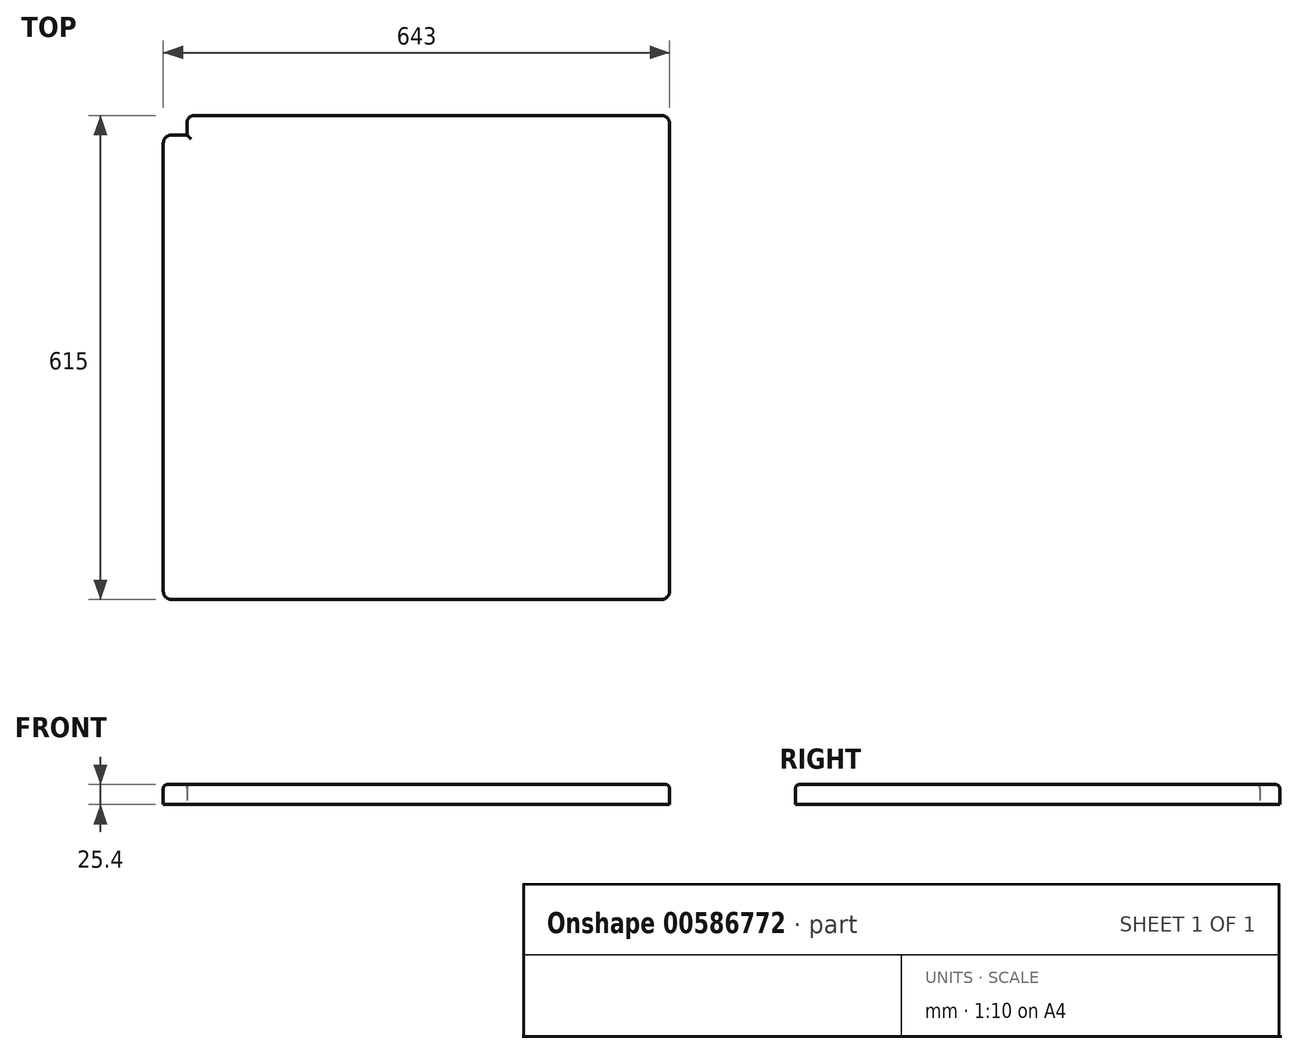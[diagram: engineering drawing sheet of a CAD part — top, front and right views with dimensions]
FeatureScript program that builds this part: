
annotation { "Feature Type Name" : "Feature", "Feature Type Description" : "" }
export const myFeature = defineFeature(function(context is Context, id is Id, definition is map)
    precondition{}
    {
        {
            var Q0;
            Q0=qCreatedBy(makeId("Top.planeOp"),FACE);
            var sketch = newSketch(context, id + "F0", { "sketchPlane" : qUnion([Q0])});
            skLineSegment(sketch, "E0.bottom", {"start": v(-281.5, 307.5) * mm, "end": v(311.5, 307.5) * mm});
            skLineSegment(sketch, "E0.top", {"start": v(-311.5, -307.5) * mm, "end": v(311.5, -307.5) * mm});
            skLineSegment(sketch, "E0.left", {"start": v(-321.5, 272.5) * mm, "end": v(-321.5, -297.5) * mm});
            skLineSegment(sketch, "E0.right", {"start": v(321.5, 297.5) * mm, "end": v(321.5, -297.5) * mm});
            skLineSegment(sketch, "E1", {"start": v(-321.5, 307.5) * mm, "end": v(321.5, -307.5) * mm, "construction": true});
            skLineSegment(sketch, "E2", {"start": v(-311.5, 282.5) * mm, "end": v(-291.5, 282.5) * mm});
            skLineSegment(sketch, "E3", {"start": v(-291.5, 282.5) * mm, "end": v(-291.5, 297.5) * mm});
            skPoint(sketch, "E4.visualSharp", {"position": v(-321.5, 282.5) * mm});
            skArc(sketch, "E4.filletArc", {"start": v(-311.5, 282.5) * mm, "mid": v(-318.57, 279.57) * mm, "end": v(-321.5, 272.5) * mm});
            skPoint(sketch, "E5.visualSharp", {"position": v(-291.5, 307.5) * mm});
            skArc(sketch, "E5.filletArc", {"start": v(-281.5, 307.5) * mm, "mid": v(-288.57, 304.57) * mm, "end": v(-291.5, 297.5) * mm});
            skPoint(sketch, "E6.visualSharp", {"position": v(321.5, 307.5) * mm});
            skArc(sketch, "E6.filletArc", {"start": v(321.5, 297.5) * mm, "mid": v(318.57, 304.57) * mm, "end": v(311.5, 307.5) * mm});
            skPoint(sketch, "E7.visualSharp", {"position": v(321.5, -307.5) * mm});
            skArc(sketch, "E7.filletArc", {"start": v(311.5, -307.5) * mm, "mid": v(318.57, -304.57) * mm, "end": v(321.5, -297.5) * mm});
            skPoint(sketch, "E8.visualSharp", {"position": v(-321.5, -307.5) * mm});
            skArc(sketch, "E8.filletArc", {"start": v(-321.5, -297.5) * mm, "mid": v(-318.57, -304.57) * mm, "end": v(-311.5, -307.5) * mm});
            skSolve(sketch);
        }
        {
            var Q0;
            Q0 = qSketchRegion(id + "F0", true);
            extrude(context, id + "F1", {"entities" : qUnion([Q0]), "depth" : 25.4 * mm, "offsetDistance" : 25.4 * mm});
        }
        {
            var Q0;
            Q0=makeQuery(id+"F1.opExtrude","CAP_EDGE",EDGE,{"disambiguationData":[OSD([sQuery(id+"F0.wireOp",EDGE,"E0.left")])],"isStart":false});
            fillet(context, id + "F2", {"entities" : qUnion([Q0]), "radius" : 5 * mm, "tangentPropagation" : true, "allowEdgeOverflow" : false});
        }
    });
